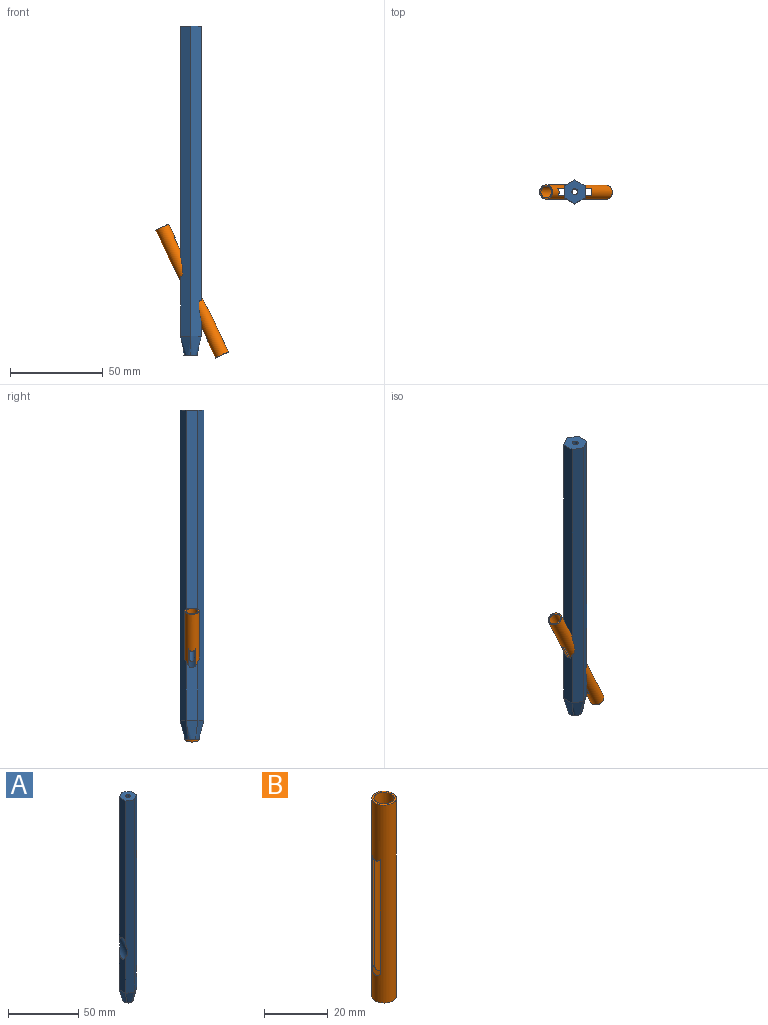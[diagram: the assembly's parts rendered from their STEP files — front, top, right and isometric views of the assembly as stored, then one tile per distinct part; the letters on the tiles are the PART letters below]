
ASSEMBLY  parts=2 mates=1
PART A: 19 faces, bbox 25.5x12.8x177.8 mm
  f0: plane 124.35x6.42mm, normal (-1,0,0), area 780.5mm2, adj f2,f4,f8,f9
  f1: plane 148.19x6.42mm, normal (1,0,0), area 933.4mm2, adj f5,f7,f8,f9
  f2: plane 167.64x5.56mm, normal (-0.5,0.87,0), area 1064.1mm2, adj f0,f3,f7,f8,f9,f13
  f3: plane 32.23x6.42mm, normal (-1,0,0), area 189.4mm2, adj f2,f4,f9,f18
  f4: plane 167.64x5.56mm, normal (-0.5,-0.87,0), area 1064.1mm2, adj f0,f3,f5,f8,f9,f17
  f5: plane 167.64x5.56mm, normal (0.5,-0.87,0), area 1064.1mm2, adj f1,f4,f6,f8,f9,f16
  f6: plane 8.4x6.42mm, normal (1,0,0), area 36.5mm2, adj f5,f7,f9,f15
  f7: plane 167.64x5.56mm, normal (0.5,0.87,0), area 1064.1mm2, adj f1,f2,f6,f8,f9,f14
  f8: plane 12.83x11.11mm, normal (0,0,1), area 99mm2, adj f0,f1,f2,f4,f5,f7,f10
  f9: cylinder r=3.97mm len=42.63mm, axis (0.42,0,-0.91), area 576.1mm2, adj f0,f1,f2,f3,f4,f5,f6,f7
  f10: cylinder r=1.59mm len=135.81mm, axis (0,0,-1), area 1324.6mm2, adj f8,f9
  f11: cylinder r=1.59mm len=30.01mm, axis (0,0,-1), area 269.3mm2, adj f9,f12
  f12: plane 7.44x7.44mm, normal (0,0,-1), area 35.5mm2, adj f11,f13,f14,f15,f16,f17,f18
  f13: bspline ~10.16x5.56mm, area 53.1mm2, adj f2,f12,f14,f18
  f14: bspline ~10.16x5.56mm, area 53.1mm2, adj f7,f12,f13,f15
  f15: bspline ~10.16x6.42mm, area 53.1mm2, adj f6,f12,f14,f16
  f16: bspline ~10.16x5.56mm, area 53.1mm2, adj f5,f12,f15,f17
  f17: bspline ~10.16x5.56mm, area 53.1mm2, adj f4,f12,f16,f18
  f18: bspline ~10.16x6.42mm, area 53.1mm2, adj f3,f12,f13,f17
PART B: 14 faces, bbox 7.7x7.7x76.2 mm
  f0: cylinder r=3.17mm len=76.2mm, axis (0,0,-1), area 1187.3mm2, adj f2,f3,f4,f5,f6,f7,f8,f9
  f1: cylinder r=3.87mm len=76.2mm, axis (0,0,-1), area 1535.8mm2, adj f2,f3,f4,f5,f6,f7,f10,f11
  f2: plane 7.75x7.75mm, normal (0,0,1), area 15.5mm2, adj f0,f1
  f3: plane 7.75x7.75mm, normal (0,0,-1), area 15.5mm2, adj f0,f1
  f4: plane 3.58x1.04mm, normal (-0.42,0,-0.91), area 2.8mm2, adj f0,f1,f5,f6,f8,f9
  f5: plane 44.47x0.81mm, normal (0,1,0), area 35.3mm2, adj f0,f1,f4,f7,f8
  f6: plane 44.48x0.81mm, normal (0,-1,0), area 35.3mm2, adj f0,f1,f4,f7,f9
  f7: plane 3.58x2.68mm, normal (-0.91,0,0.42), area 6.2mm2, adj f0,f1,f5,f6
  f8: plane 0.46x0.36mm, normal (0.91,0,-0.42), area 0.1mm2, adj f0,f4,f5
  f9: plane 0.46x0.37mm, normal (0.91,0,-0.42), area 0.1mm2, adj f0,f4,f6
  f10: plane 3.58x2.68mm, normal (-0.91,0,0.42), area 6.2mm2, adj f0,f1,f11,f13
  f11: plane 45.76x0.81mm, normal (0,-1,0), area 35.8mm2, adj f0,f1,f10,f12
  f12: plane 3.58x2.68mm, normal (0.91,0,-0.42), area 6.2mm2, adj f0,f1,f11,f13
  f13: plane 45.76x0.81mm, normal (0,1,0), area 35.8mm2, adj f0,f1,f10,f12
PLACE A t=(-75.92,38.61,-36)mm
PLACE B rot(axis=(0,-1,0),25deg) t=(-59.18,38.61,-46.06)mm
MATE slider B.f1 <-> A.f9  axis (0.42,0,-0.91) through (-75.28,38.61,-11.53)mm
